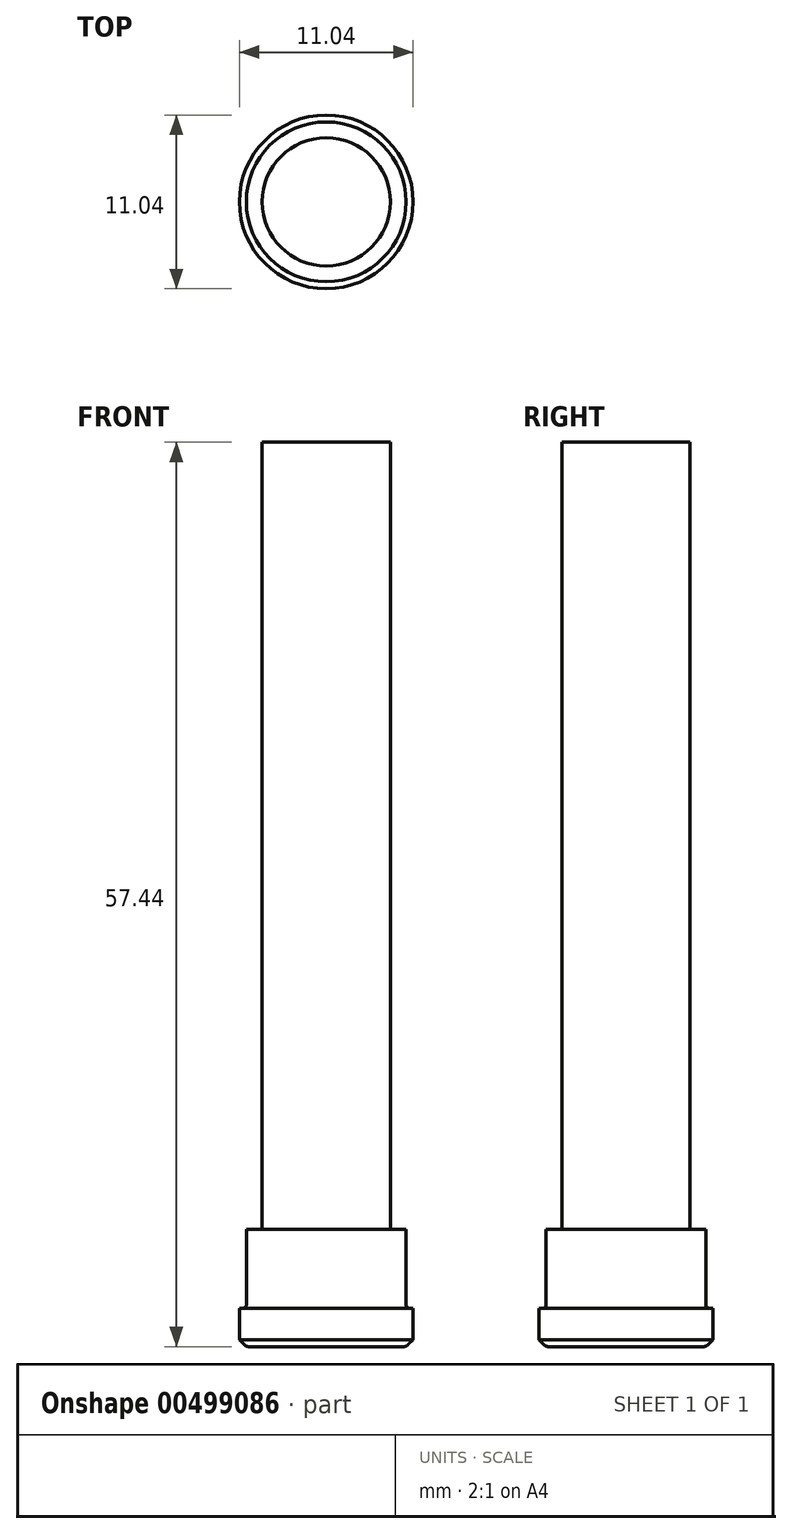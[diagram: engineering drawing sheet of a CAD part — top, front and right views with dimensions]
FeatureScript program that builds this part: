
annotation { "Feature Type Name" : "Feature", "Feature Type Description" : "" }
export const myFeature = defineFeature(function(context is Context, id is Id, definition is map)
    precondition{}
    {
        {
            var Q0;
            Q0=qCreatedBy(makeId("Front.planeOp"),FACE);
            var sketch = newSketch(context, id + "F0", { "sketchPlane" : qUnion([Q0])});
            skLineSegment(sketch, "E0", {"start": v(0, 0) * mm, "end": v(4.08, 0) * mm});
            skLineSegment(sketch, "E1", {"start": v(4.08, 0) * mm, "end": v(4.08, -50) * mm});
            skLineSegment(sketch, "E2", {"start": v(4.08, -50) * mm, "end": v(5.08, -50) * mm});
            skLineSegment(sketch, "E3", {"start": v(5.08, -50) * mm, "end": v(5.08, -54.8) * mm});
            skLineSegment(sketch, "E4", {"start": v(5.28, -55) * mm, "end": v(5.52, -55) * mm});
            skPoint(sketch, "E5", {"position": v(5.08, -54.8) * mm});
            skPoint(sketch, "E6", {"position": v(5.28, -55) * mm});
            skArc(sketch, "E7", {"start": v(5.08, -54.8) * mm, "mid": v(5.13, -54.94) * mm, "end": v(5.28, -55) * mm});
            skLineSegment(sketch, "E8", {"start": v(5.52, -55) * mm, "end": v(5.52, -57) * mm});
            skLineSegment(sketch, "E9", {"start": v(5.52, -57) * mm, "end": v(5.16, -57.35) * mm});
            skLineSegment(sketch, "E10", {"start": v(5.08, -57.41) * mm, "end": v(5.08, -57.44) * mm});
            skLineSegment(sketch, "E11", {"start": v(0, 0) * mm, "end": v(0, -57.44) * mm});
            skLineSegment(sketch, "E12", {"start": v(4.95, -57.44) * mm, "end": v(0, -57.44) * mm});
            skPoint(sketch, "E13.visualSharp", {"position": v(5.08, -57.44) * mm});
            skArc(sketch, "E13.filletArc", {"start": v(4.95, -57.44) * mm, "mid": v(5.07, -57.42) * mm, "end": v(5.16, -57.35) * mm});
            skSolve(sketch);
        }
        {
            var Q0;
            Q0=makeQuery(id+"F0.imprint","IMPRINT",FACE,{"disambiguationData":[TD([[makeQuery(id+"F0.imprint","IMPRINT",EDGE,{"derivedFrom":sQuery(id+"F0.wireOp",EDGE,"E0")}),-1.0]])]});
            var Q1;
            Q1=sQuery(id+"F0.wireOp",EDGE,"E11");
            revolve(context, id + "F1", {"entities" : qUnion([Q0]), "axis" : qUnion([Q1]), "revolveType" : RevolveType.FULL});
        }
    });
